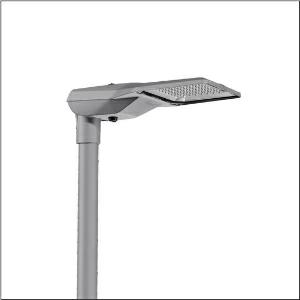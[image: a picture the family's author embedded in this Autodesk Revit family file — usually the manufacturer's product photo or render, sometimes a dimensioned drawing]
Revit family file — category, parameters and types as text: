
# Revit family: streetlight_sl_21_midi___st0_5a_5xe3b43t08mb_3943
name_source: partatom
category: Lighting Fixtures
units: mm (PartAtom-declared; Revit-internal decimal feet)

## family parameters
Cut with Voids When Loaded = No
Host = Face
Light Source = No
Part Type = Normal
Room Calculation Point = No
Round Connector Dimension = Use Diameter
Shared = No

## types (1)
- --- (1 x LED, 20180 lm, 147 W, 4000K)
    Apparent Load = 147 VA
    CIE Flux Codes = 41 75 97 100 100
    Color Rendering = 70
    Color Temperature = 4000K
    Default Elevation = 1800 mm
    Description = Streetlight SL 21 midi, mast luminaire, primary light control with lens, of PMMA, primary optical cover: cover, of toughened safety glass, transparent, light distribution: ST0.5a, light emission: direct distribution, primary light characteristic: asymmetric, installation type: side-entry, post-top, LED, High Power LED, rated luminous flux: 20.180lm, luminous efficacy: 137lm/W, light colour: 740, colour temperature: 4000K, control: overheat protection, constant luminous flux control, time-dependent luminous flux control, flexible luminous flux parameterisation, presetting dimming logarithmic, mains connection: 230..240V, AC, 50/60Hz, start of lifetime: 147W, end of service life: 155W, reduction: 65W, luminaire housing, of diecast aluminium, powder-coated, Siteco® metallic grey (DB 702S), corrosivity category C5 mid according to DIN EN ISO 12944, please order mast flange separately, inclination adjustable: 0°, 5°, 10°, 15°, sealing non-destructively replaceable, multi-level sealing system, length: 644mm, width: 335mm, height: 110mm, mast flange for spigot size: 42mm (side-entry): 5XC10008XM4, 60/48mm (side-entry/post-top): 5XC10108XM2, 76/60mm (side-entry/post-top): 5XC10108XM1, Smart Interface below and above, protection rating (complete): IP66, insulation class (complete): insulation class II (safety insulation), certification: CE, ENEC, ENEC+, VDE, impact resistance: IK09, permissible operating ambient temperature for outdoor applications: -40..+50°C, standard-compliant lighting for roads and squares, packaging unit: 1 piece

Light Distribution: ST0.5a
    Height = 111 mm
    Lamp = 1 x LED
    Lamp Light Flux = 20180 lm
    Lamp Power = 147 W
    Lamp count = 1
    Length = 644 mm
    Luminous efficacy = 137 lm/W
    Manufacturer = Siteco
    ModVariant = No
    Model = 5XE3B43T08MB
    Number of Poles = 1
    OnlyDefault = Yes
    Power Factor = 1
    Product Name = Streetlight SL 21 midi | ST0.5a
    Product group = mast luminaire | pylon top
    ProductGroupID = 6100
    Protection Class = Protection class II
    Protection Degree = IP 66
    RLX_Detail_Level = 1
    RLX_Emergency_Light_Flux = 0 lm
    RLX_Emergency_Type = 0
    RLX_Emergency_Type_DB = No
    RlxData = <blob elided: 101573 chars, md5=ebe36cac>
    Socket = socket
    Standby Power = 0 W
    System Light Flux = 20180 lm
    System Power = 147 W
    Type Comments = factory setting: luminous flux: 100 % | dim-lin: 254 | 750 mA
    Type Image = l_1004304.jpg
    URL = http://relux.com
    VarID = @adj_144083
    Voltage = 0 V
    Weight = 0.00 kg
    Width = 336 mm

## geometry (parser evidence)
native form markers: Blend x4, Sweep x11
no freeform markers — native parametric forms only
